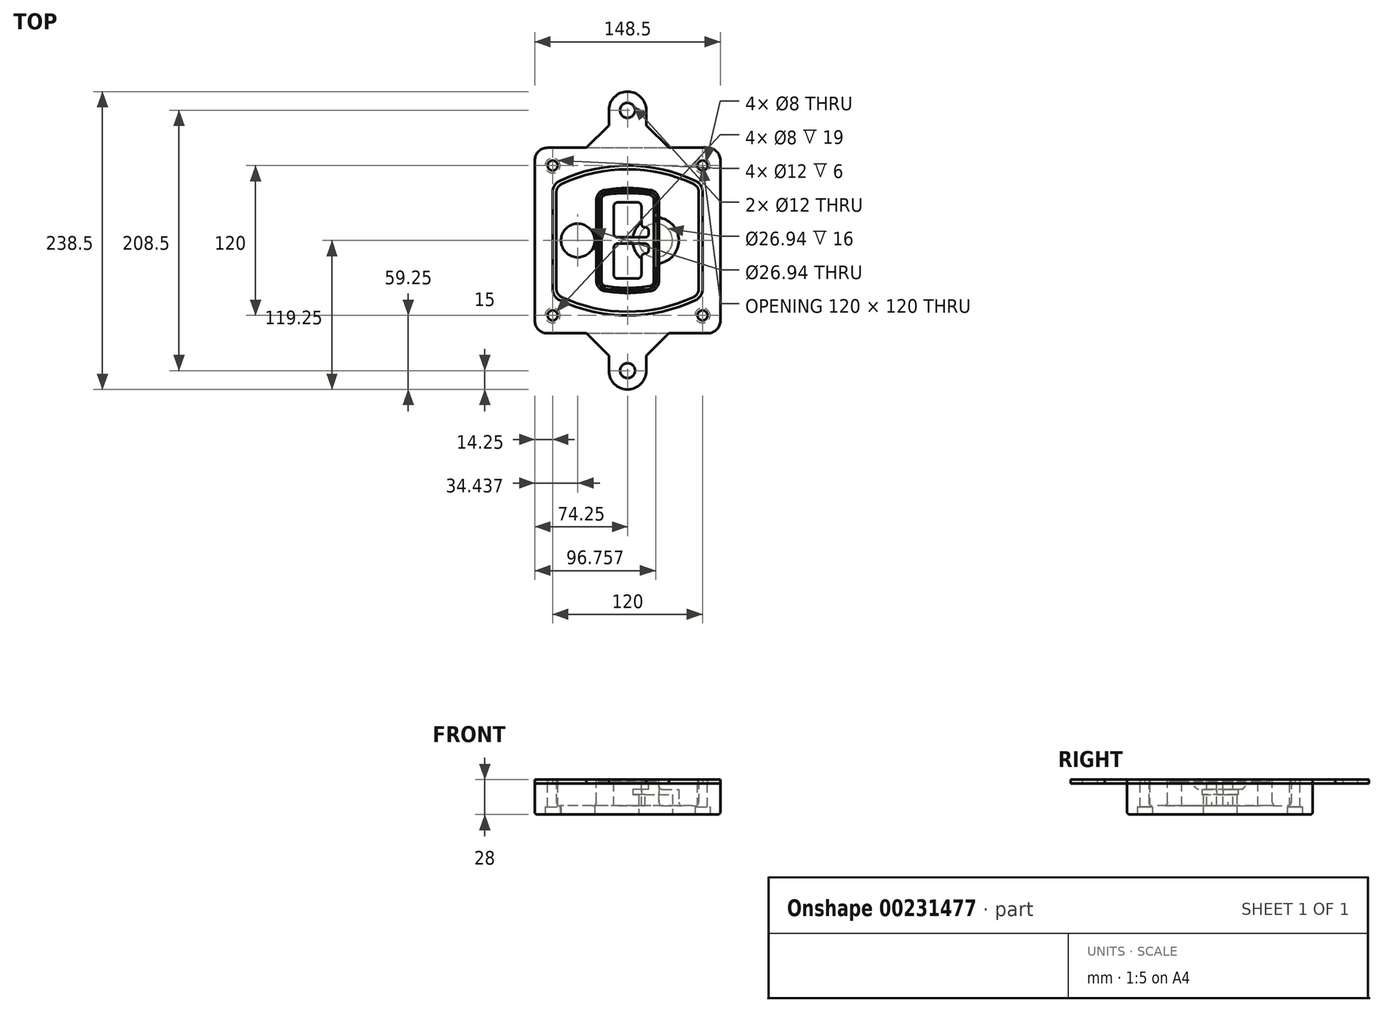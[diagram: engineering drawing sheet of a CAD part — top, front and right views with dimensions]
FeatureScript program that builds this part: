
annotation { "Feature Type Name" : "Feature", "Feature Type Description" : "" }
export const myFeature = defineFeature(function(context is Context, id is Id, definition is map)
    precondition{}
    {
        {
            var Q0;
            Q0=qCreatedBy(makeId("Top.planeOp"),FACE);
            var sketch = newSketch(context, id + "F0", { "sketchPlane" : qUnion([Q0])});
            skPoint(sketch, "E0.rect.middle", {"position": v(0, 0) * mm});
            skLineSegment(sketch, "E1.bottom", {"start": v(-64.25, -74.25) * mm, "end": v(64.25, -74.25) * mm});
            skLineSegment(sketch, "E1.top", {"start": v(-64.25, 74.25) * mm, "end": v(64.25, 74.25) * mm});
            skLineSegment(sketch, "E1.left", {"start": v(-74.25, -64.25) * mm, "end": v(-74.25, 64.25) * mm});
            skLineSegment(sketch, "E1.right", {"start": v(74.25, -64.25) * mm, "end": v(74.25, 64.25) * mm});
            skLineSegment(sketch, "E2", {"start": v(-74.25, 74.25) * mm, "end": v(74.25, -74.25) * mm, "construction": true});
            skLineSegment(sketch, "E3", {"start": v(74.25, 74.25) * mm, "end": v(-74.25, -74.25) * mm, "construction": true});
            skCircle(sketch, "E4", {"center": v(-60, 60) * mm, "radius": 4 * mm});
            skCircle(sketch, "E5", {"center": v(60, 60) * mm, "radius": 4 * mm});
            skCircle(sketch, "E6", {"center": v(60, -60) * mm, "radius": 4 * mm});
            skCircle(sketch, "E7", {"center": v(-60, -60) * mm, "radius": 4 * mm});
            skLineSegment(sketch, "E8", {"start": v(-60, 60) * mm, "end": v(60, 60) * mm, "construction": true});
            skLineSegment(sketch, "E9", {"start": v(60, 60) * mm, "end": v(60, -60) * mm, "construction": true});
            skLineSegment(sketch, "E10", {"start": v(60, -60) * mm, "end": v(-60, -60) * mm, "construction": true});
            skLineSegment(sketch, "E11", {"start": v(-60, -60) * mm, "end": v(-60, 60) * mm, "construction": true});
            skLineSegment(sketch, "E12", {"start": v(-60, 38.83) * mm, "end": v(-60, -38.83) * mm});
            skLineSegment(sketch, "E13", {"start": v(60, 38.83) * mm, "end": v(60, -38.83) * mm});
            skArc(sketch, "E14", {"start": v(54.26, 47.88) * mm, "mid": v(0, 60) * mm, "end": v(-54.26, 47.88) * mm});
            skArc(sketch, "E15", {"start": v(-54.26, -47.88) * mm, "mid": v(0, -60) * mm, "end": v(54.26, -47.88) * mm});
            skLineSegment(sketch, "E16", {"start": v(-60, 0) * mm, "end": v(60, 0) * mm, "construction": true});
            skPoint(sketch, "E17.visualSharp", {"position": v(-60, -45) * mm});
            skArc(sketch, "E17.filletArc", {"start": v(-60, -38.83) * mm, "mid": v(-58.44, -44.2) * mm, "end": v(-54.26, -47.88) * mm});
            skPoint(sketch, "E18.visualSharp", {"position": v(-60, 45) * mm});
            skArc(sketch, "E18.filletArc", {"start": v(-54.26, 47.88) * mm, "mid": v(-58.44, 44.2) * mm, "end": v(-60, 38.83) * mm});
            skPoint(sketch, "E19.visualSharp", {"position": v(60, 45) * mm});
            skArc(sketch, "E19.filletArc", {"start": v(60, 38.83) * mm, "mid": v(58.44, 44.2) * mm, "end": v(54.26, 47.88) * mm});
            skPoint(sketch, "E20.visualSharp", {"position": v(60, -45) * mm});
            skArc(sketch, "E20.filletArc", {"start": v(54.26, -47.88) * mm, "mid": v(58.44, -44.2) * mm, "end": v(60, -38.83) * mm});
            skPoint(sketch, "E21.visualSharp", {"position": v(-74.25, 74.25) * mm});
            skArc(sketch, "E21.filletArc", {"start": v(-64.25, 74.25) * mm, "mid": v(-71.32, 71.32) * mm, "end": v(-74.25, 64.25) * mm});
            skPoint(sketch, "E22.visualSharp", {"position": v(74.25, 74.25) * mm});
            skArc(sketch, "E22.filletArc", {"start": v(74.25, 64.25) * mm, "mid": v(71.32, 71.32) * mm, "end": v(64.25, 74.25) * mm});
            skPoint(sketch, "E23.visualSharp", {"position": v(74.25, -74.25) * mm});
            skArc(sketch, "E23.filletArc", {"start": v(64.25, -74.25) * mm, "mid": v(71.32, -71.32) * mm, "end": v(74.25, -64.25) * mm});
            skPoint(sketch, "E24.visualSharp", {"position": v(-74.25, -74.25) * mm});
            skArc(sketch, "E24.filletArc", {"start": v(-74.25, -64.25) * mm, "mid": v(-71.32, -71.32) * mm, "end": v(-64.25, -74.25) * mm});
            skArc(sketch, "E25.0", {"start": v(57, 38.83) * mm, "mid": v(55.9, 42.58) * mm, "end": v(52.98, 45.17) * mm});
            skLineSegment(sketch, "E25.1", {"start": v(57, 38.83) * mm, "end": v(57, -38.83) * mm});
            skArc(sketch, "E25.2", {"start": v(52.98, -45.17) * mm, "mid": v(55.9, -42.58) * mm, "end": v(57, -38.83) * mm});
            skArc(sketch, "E25.3", {"start": v(-52.98, -45.17) * mm, "mid": v(0, -57) * mm, "end": v(52.98, -45.17) * mm});
            skArc(sketch, "E25.4", {"start": v(-57, -38.83) * mm, "mid": v(-55.9, -42.58) * mm, "end": v(-52.98, -45.17) * mm});
            skArc(sketch, "E25.5", {"start": v(52.98, 45.17) * mm, "mid": v(0, 57) * mm, "end": v(-52.98, 45.17) * mm});
            skLineSegment(sketch, "E25.6", {"start": v(-57, 38.83) * mm, "end": v(-57, -38.83) * mm});
            skArc(sketch, "E25.7", {"start": v(-52.98, 45.17) * mm, "mid": v(-55.9, 42.58) * mm, "end": v(-57, 38.83) * mm});
            skArc(sketch, "E26.0", {"start": v(-55.96, 51.5) * mm, "mid": v(-61.82, 46.33) * mm, "end": v(-64, 38.83) * mm});
            skArc(sketch, "E26.1", {"start": v(55.96, 51.5) * mm, "mid": v(0, 64) * mm, "end": v(-55.96, 51.5) * mm});
            skArc(sketch, "E26.2", {"start": v(64, 38.83) * mm, "mid": v(61.82, 46.33) * mm, "end": v(55.96, 51.5) * mm});
            skLineSegment(sketch, "E26.3", {"start": v(64, 38.83) * mm, "end": v(64, -38.83) * mm});
            skArc(sketch, "E26.4", {"start": v(55.96, -51.5) * mm, "mid": v(61.82, -46.33) * mm, "end": v(64, -38.83) * mm});
            skLineSegment(sketch, "E26.5", {"start": v(-64, 38.83) * mm, "end": v(-64, -38.83) * mm});
            skArc(sketch, "E26.6", {"start": v(-55.96, -51.5) * mm, "mid": v(0, -64) * mm, "end": v(55.96, -51.5) * mm});
            skArc(sketch, "E26.7", {"start": v(-64, -38.83) * mm, "mid": v(-61.82, -46.33) * mm, "end": v(-55.96, -51.5) * mm});
            skSolve(sketch);
        }
        {
            var Q0;
            Q0=makeQuery(id+"F0.imprint","IMPRINT",FACE,{"disambiguationData":[TD([[makeQuery(id+"F0.imprint","IMPRINT",EDGE,{"derivedFrom":sQuery(id+"F0.wireOp",EDGE,"E1.bottom")}),1.0]])]});
            var Q1;
            Q1=makeQuery(id+"F0.imprint","IMPRINT",FACE,{"disambiguationData":[TD([[makeQuery(id+"F0.imprint","IMPRINT",EDGE,{"derivedFrom":sQuery(id+"F0.wireOp",EDGE,"E12")}),1.0]])]});
            var Q2;
            Q2=makeQuery(id+"F0.imprint","IMPRINT",FACE,{"disambiguationData":[TD([[makeQuery(id+"F0.imprint","IMPRINT",EDGE,{"derivedFrom":sQuery(id+"F0.wireOp",EDGE,"E25.0")}),1.0]])]});
            var Q3;
            Q3=makeQuery(id+"F0.imprint","IMPRINT",FACE,{"disambiguationData":[TD([[makeQuery(id+"F0.imprint","IMPRINT",EDGE,{"derivedFrom":sQuery(id+"F0.wireOp",EDGE,"E12")}),-1.0]])]});
            extrude(context, id + "F1", {"entities" : qUnion([Q0, Q1, Q2, Q3]), "oppositeDirection" : true, "depth" : 25 * mm});
        }
        {
            var Q0;
            Q0=makeQuery(id+"F0.imprint","IMPRINT",FACE,{"disambiguationData":[TD([[makeQuery(id+"F0.imprint","IMPRINT",EDGE,{"derivedFrom":sQuery(id+"F0.wireOp",EDGE,"E12")}),1.0]])]});
            extrude(context, id + "F2", {"entities" : qUnion([Q0]), "operationType" : NewBodyOperationType.ADD, "depth" : 3 * mm});
        }
        {
            var Q0;
            Q0=makeQuery(id+"F0.imprint","IMPRINT",FACE,{"disambiguationData":[TD([[makeQuery(id+"F0.imprint","IMPRINT",EDGE,{"derivedFrom":sQuery(id+"F0.wireOp",EDGE,"E25.0")}),1.0]])]});
            extrude(context, id + "F3", {"entities" : qUnion([Q0]), "operationType" : NewBodyOperationType.REMOVE, "oppositeDirection" : true, "depth" : 18 * mm});
        }
        {
            var Q0;
            Q0=makeQuery(id+"F2.opExtrude","CAP_FACE",FACE,{"disambiguationData":[OSD([sQuery(id+"F0.wireOp",EDGE,"E12"),sQuery(id+"F0.wireOp",EDGE,"E13"),sQuery(id+"F0.wireOp",EDGE,"E14"),sQuery(id+"F0.wireOp",EDGE,"E15"),sQuery(id+"F0.wireOp",EDGE,"E17.filletArc"),sQuery(id+"F0.wireOp",EDGE,"E18.filletArc"),sQuery(id+"F0.wireOp",EDGE,"E19.filletArc"),sQuery(id+"F0.wireOp",EDGE,"E20.filletArc"),sQuery(id+"F0.wireOp",EDGE,"E25.0"),sQuery(id+"F0.wireOp",EDGE,"E25.1"),sQuery(id+"F0.wireOp",EDGE,"E25.2"),sQuery(id+"F0.wireOp",EDGE,"E25.3"),sQuery(id+"F0.wireOp",EDGE,"E25.4"),sQuery(id+"F0.wireOp",EDGE,"E25.5"),sQuery(id+"F0.wireOp",EDGE,"E25.6"),sQuery(id+"F0.wireOp",EDGE,"E25.7")])],"isStart":false});
            var sketch = newSketch(context, id + "F4", { "sketchPlane" : qUnion([Q0])});
            skArc(sketch, "E27.0", {"start": v(-18.34, -40.45) * mm, "mid": v(0, -42) * mm, "end": v(18.34, -40.45) * mm});
            skArc(sketch, "E28.0", {"start": v(18.34, 40.45) * mm, "mid": v(0, 42) * mm, "end": v(-18.34, 40.45) * mm});
            skLineSegment(sketch, "E29", {"start": v(-25, 32.57) * mm, "end": v(-25, -32.57) * mm});
            skLineSegment(sketch, "E30", {"start": v(25, 32.57) * mm, "end": v(25, -32.57) * mm});
            skLineSegment(sketch, "E31", {"start": v(-25, 39.1) * mm, "end": v(25, 39.1) * mm, "construction": true});
            skLineSegment(sketch, "E32", {"start": v(-25, -39.1) * mm, "end": v(25, -39.1) * mm, "construction": true});
            skPoint(sketch, "E33.visualSharp", {"position": v(-25, 39.1) * mm});
            skArc(sketch, "E33.filletArc", {"start": v(-18.34, 40.45) * mm, "mid": v(-23.11, 37.73) * mm, "end": v(-25, 32.57) * mm});
            skPoint(sketch, "E34.visualSharp", {"position": v(25, 39.1) * mm});
            skArc(sketch, "E34.filletArc", {"start": v(25, 32.57) * mm, "mid": v(23.11, 37.73) * mm, "end": v(18.34, 40.45) * mm});
            skPoint(sketch, "E35.visualSharp", {"position": v(25, -39.1) * mm});
            skArc(sketch, "E35.filletArc", {"start": v(18.34, -40.45) * mm, "mid": v(23.11, -37.73) * mm, "end": v(25, -32.57) * mm});
            skPoint(sketch, "E36.visualSharp", {"position": v(-25, -39.1) * mm});
            skArc(sketch, "E36.filletArc", {"start": v(-25, -32.57) * mm, "mid": v(-23.11, -37.73) * mm, "end": v(-18.34, -40.45) * mm});
            skArc(sketch, "E37.0", {"start": v(52.98, 45.17) * mm, "mid": v(0, 57) * mm, "end": v(-52.98, 45.17) * mm});
            skArc(sketch, "E37.1", {"start": v(-52.98, 45.17) * mm, "mid": v(-55.9, 42.58) * mm, "end": v(-57, 38.83) * mm});
            skLineSegment(sketch, "E37.2", {"start": v(-57, 38.83) * mm, "end": v(-57, -38.83) * mm});
            skArc(sketch, "E37.3", {"start": v(-57, -38.83) * mm, "mid": v(-55.9, -42.58) * mm, "end": v(-52.98, -45.17) * mm});
            skArc(sketch, "E37.4", {"start": v(-52.98, -45.17) * mm, "mid": v(0, -57) * mm, "end": v(52.98, -45.17) * mm});
            skArc(sketch, "E37.5", {"start": v(52.98, -45.17) * mm, "mid": v(55.9, -42.58) * mm, "end": v(57, -38.83) * mm});
            skLineSegment(sketch, "E37.6", {"start": v(57, 38.83) * mm, "end": v(57, -38.83) * mm});
            skArc(sketch, "E37.7", {"start": v(57, 38.83) * mm, "mid": v(55.9, 42.58) * mm, "end": v(52.98, 45.17) * mm});
            skLineSegment(sketch, "E38.0", {"start": v(23, 32.57) * mm, "end": v(23, -32.57) * mm});
            skArc(sketch, "E38.1", {"start": v(18, -38.48) * mm, "mid": v(21.58, -36.44) * mm, "end": v(23, -32.57) * mm});
            skArc(sketch, "E38.2", {"start": v(-18, -38.48) * mm, "mid": v(0, -40) * mm, "end": v(18, -38.48) * mm});
            skArc(sketch, "E38.3", {"start": v(-23, -32.57) * mm, "mid": v(-21.58, -36.44) * mm, "end": v(-18, -38.48) * mm});
            skLineSegment(sketch, "E38.4", {"start": v(-23, 32.57) * mm, "end": v(-23, -32.57) * mm});
            skArc(sketch, "E38.5", {"start": v(23, 32.57) * mm, "mid": v(21.58, 36.44) * mm, "end": v(18, 38.48) * mm});
            skArc(sketch, "E38.6", {"start": v(-18, 38.48) * mm, "mid": v(-21.58, 36.44) * mm, "end": v(-23, 32.57) * mm});
            skArc(sketch, "E38.7", {"start": v(18, 38.48) * mm, "mid": v(0, 40) * mm, "end": v(-18, 38.48) * mm});
            skArc(sketch, "E39.0", {"start": v(21, 32.57) * mm, "mid": v(20.06, 35.15) * mm, "end": v(17.67, 36.5) * mm});
            skLineSegment(sketch, "E39.1", {"start": v(21, 32.57) * mm, "end": v(21, -32.57) * mm});
            skArc(sketch, "E39.2", {"start": v(17.67, -36.5) * mm, "mid": v(20.06, -35.15) * mm, "end": v(21, -32.57) * mm});
            skArc(sketch, "E39.3", {"start": v(-17.67, -36.5) * mm, "mid": v(0, -38) * mm, "end": v(17.67, -36.5) * mm});
            skArc(sketch, "E39.4", {"start": v(-21, -32.57) * mm, "mid": v(-20.06, -35.15) * mm, "end": v(-17.67, -36.5) * mm});
            skArc(sketch, "E39.5", {"start": v(17.67, 36.5) * mm, "mid": v(0, 38) * mm, "end": v(-17.67, 36.5) * mm});
            skLineSegment(sketch, "E39.6", {"start": v(-21, 32.57) * mm, "end": v(-21, -32.57) * mm});
            skArc(sketch, "E39.7", {"start": v(-17.67, 36.5) * mm, "mid": v(-20.06, 35.15) * mm, "end": v(-21, 32.57) * mm});
            skLineSegment(sketch, "E40", {"start": v(-25, 0) * mm, "end": v(25, 0) * mm, "construction": true});
            skLineSegment(sketch, "E41", {"start": v(-11, 5.5) * mm, "end": v(-11, 27.5) * mm});
            skLineSegment(sketch, "E42", {"start": v(-8, 30.5) * mm, "end": v(8, 30.5) * mm});
            skLineSegment(sketch, "E43", {"start": v(11, 27.5) * mm, "end": v(11, 13.5) * mm});
            skLineSegment(sketch, "E44", {"start": v(14, 10.5) * mm, "end": v(14, 10.5) * mm});
            skLineSegment(sketch, "E45", {"start": v(17, 7.5) * mm, "end": v(17, 5.5) * mm});
            skLineSegment(sketch, "E46", {"start": v(14, 2.5) * mm, "end": v(-8, 2.5) * mm});
            skPoint(sketch, "E47.visualSharp", {"position": v(-11, 30.5) * mm});
            skArc(sketch, "E47.filletArc", {"start": v(-8, 30.5) * mm, "mid": v(-10.12, 29.62) * mm, "end": v(-11, 27.5) * mm});
            skPoint(sketch, "E48.visualSharp", {"position": v(11, 30.5) * mm});
            skArc(sketch, "E48.filletArc", {"start": v(11, 27.5) * mm, "mid": v(10.12, 29.62) * mm, "end": v(8, 30.5) * mm});
            skPoint(sketch, "E49.visualSharp", {"position": v(11, 10.5) * mm});
            skArc(sketch, "E49.filletArc", {"start": v(11, 13.5) * mm, "mid": v(11.88, 11.38) * mm, "end": v(14, 10.5) * mm});
            skPoint(sketch, "E50.visualSharp", {"position": v(17, 10.5) * mm});
            skArc(sketch, "E50.filletArc", {"start": v(17, 7.5) * mm, "mid": v(16.12, 9.62) * mm, "end": v(14, 10.5) * mm});
            skPoint(sketch, "E51.visualSharp", {"position": v(17, 2.5) * mm});
            skArc(sketch, "E51.filletArc", {"start": v(14, 2.5) * mm, "mid": v(16.12, 3.38) * mm, "end": v(17, 5.5) * mm});
            skPoint(sketch, "E52.visualSharp", {"position": v(-11, 2.5) * mm});
            skArc(sketch, "E52.filletArc", {"start": v(-11, 5.5) * mm, "mid": v(-10.12, 3.38) * mm, "end": v(-8, 2.5) * mm});
            skLineSegment(sketch, "E53.0.MirrorCS", {"start": v(14, -2.5) * mm, "end": v(-8, -2.5) * mm});
            skArc(sketch, "E54.0.MirrorCS", {"start": v(-11, -5.5) * mm, "mid": v(-10.12, -3.38) * mm, "end": v(-8, -2.5) * mm});
            skLineSegment(sketch, "E55.0.MirrorCS", {"start": v(-11, -5.5) * mm, "end": v(-11, -27.5) * mm});
            skArc(sketch, "E56.0.MirrorCS", {"start": v(-8, -30.5) * mm, "mid": v(-10.12, -29.62) * mm, "end": v(-11, -27.5) * mm});
            skLineSegment(sketch, "E57.0.MirrorCS", {"start": v(-8, -30.5) * mm, "end": v(8, -30.5) * mm});
            skArc(sketch, "E58.0.MirrorCS", {"start": v(11, -27.5) * mm, "mid": v(10.12, -29.62) * mm, "end": v(8, -30.5) * mm});
            skLineSegment(sketch, "E59.0.MirrorCS", {"start": v(11, -27.5) * mm, "end": v(11, -13.5) * mm});
            skArc(sketch, "E60.0.MirrorCS", {"start": v(11, -13.5) * mm, "mid": v(11.88, -11.38) * mm, "end": v(14, -10.5) * mm});
            skArc(sketch, "E61.0.MirrorCS", {"start": v(17, -7.5) * mm, "mid": v(16.12, -9.62) * mm, "end": v(14, -10.5) * mm});
            skLineSegment(sketch, "E62.0.MirrorCS", {"start": v(17, -7.5) * mm, "end": v(17, -5.5) * mm});
            skArc(sketch, "E63.0.MirrorCS", {"start": v(14, -2.5) * mm, "mid": v(16.12, -3.38) * mm, "end": v(17, -5.5) * mm});
            skSolve(sketch);
        }
        {
            var Q0;
            Q0=makeQuery(id+"F4.imprint","IMPRINT",FACE,{"disambiguationData":[TD([[makeQuery(id+"F4.imprint","IMPRINT",EDGE,{"derivedFrom":sQuery(id+"F4.wireOp",EDGE,"E27.0")}),1.0]])]});
            var Q1;
            Q1=makeQuery(id+"F4.imprint","IMPRINT",FACE,{"disambiguationData":[TD([[makeQuery(id+"F4.imprint","IMPRINT",EDGE,{"derivedFrom":sQuery(id+"F4.wireOp",EDGE,"E38.0")}),-1.0]])]});
            var Q2;
            Q2=makeQuery(id+"F4.imprint","IMPRINT",FACE,{"disambiguationData":[TD([[makeQuery(id+"F4.imprint","IMPRINT",EDGE,{"derivedFrom":sQuery(id+"F4.wireOp",EDGE,"E39.0")}),1.0]])]});
            extrude(context, id + "F5", {"entities" : qUnion([Q0, Q1, Q2]), "operationType" : NewBodyOperationType.ADD, "endBound" : BoundingType.UP_TO_NEXT, "oppositeDirection" : true, "depth" : 25 * mm});
        }
        {
            var Q0;
            Q0=makeQuery(id+"F4.imprint","IMPRINT",FACE,{"disambiguationData":[TD([[makeQuery(id+"F4.imprint","IMPRINT",EDGE,{"derivedFrom":sQuery(id+"F4.wireOp",EDGE,"E38.0")}),-1.0]])]});
            extrude(context, id + "F6", {"entities" : qUnion([Q0]), "operationType" : NewBodyOperationType.REMOVE, "oppositeDirection" : true, "depth" : 2 * mm});
        }
        {
            var Q0;
            Q0=makeQuery(id+"F1.opExtrude","CAP_FACE",FACE,{"disambiguationData":[OSD([sQuery(id+"F0.wireOp",EDGE,"E1.bottom"),sQuery(id+"F0.wireOp",EDGE,"E1.top"),sQuery(id+"F0.wireOp",EDGE,"E1.left"),sQuery(id+"F0.wireOp",EDGE,"E1.right"),sQuery(id+"F0.wireOp",EDGE,"E4"),sQuery(id+"F0.wireOp",EDGE,"E5"),sQuery(id+"F0.wireOp",EDGE,"E6"),sQuery(id+"F0.wireOp",EDGE,"E7"),sQuery(id+"F0.wireOp",EDGE,"E21.filletArc"),sQuery(id+"F0.wireOp",EDGE,"E22.filletArc"),sQuery(id+"F0.wireOp",EDGE,"E23.filletArc"),sQuery(id+"F0.wireOp",EDGE,"E24.filletArc")])],"isStart":false});
            var sketch = newSketch(context, id + "F7", { "sketchPlane" : qUnion([Q0])});
            skCircle(sketch, "E64", {"center": v(22.5, 0) * mm, "radius": 13.47 * mm});
            skCircle(sketch, "E65", {"center": v(-39.81, 0) * mm, "radius": 13.47 * mm});
            skLineSegment(sketch, "E66", {"start": v(74.25, 0) * mm, "end": v(-74.25, 0) * mm});
            skCircle(sketch, "E67", {"center": v(22.5, 0) * mm, "radius": 18.47 * mm});
            skCircle(sketch, "E68", {"center": v(60, -60) * mm, "radius": 6 * mm});
            skCircle(sketch, "E69", {"center": v(-60, -60) * mm, "radius": 6 * mm});
            skCircle(sketch, "E70", {"center": v(-60, 60) * mm, "radius": 6 * mm});
            skCircle(sketch, "E71", {"center": v(60, 60) * mm, "radius": 6 * mm});
            skSolve(sketch);
        }
        {
            var Q0;
            {var subQ1=sQuery(id+"F7.wireOp",EDGE,"E66");var subQ4=sQuery(id+"F7.wireOp",EDGE,"E64");var subQ6=makeQuery(id+"F7.imprint","INTERSECT",VERTEX,{"disambiguationData":[OD(0.0)],"derivedFrom":[subQ4,subQ1]});Q0=makeQuery(id+"F7.imprint","IMPRINT",FACE,{"disambiguationData":[TD([[makeQuery(id+"F7.imprint","IMPRINT",EDGE,{"disambiguationData":[TD([[subQ6,-1.0]])],"derivedFrom":subQ4}),-1.0]])]});}
            var Q1;
            {var subQ0=sQuery(id+"F7.wireOp",EDGE,"E66");var subQ1=sQuery(id+"F7.wireOp",EDGE,"E64");var subQ3=makeQuery(id+"F7.imprint","INTERSECT",VERTEX,{"disambiguationData":[OD(0.0)],"derivedFrom":[subQ1,subQ0]});Q1=makeQuery(id+"F7.imprint","IMPRINT",FACE,{"disambiguationData":[TD([[makeQuery(id+"F7.imprint","IMPRINT",EDGE,{"disambiguationData":[TD([[subQ3,-1.0]])],"derivedFrom":subQ1}),1.0]])]});}
            var Q2;
            {var subQ0=sQuery(id+"F7.wireOp",EDGE,"E66");var subQ1=sQuery(id+"F7.wireOp",EDGE,"E64");var subQ3=makeQuery(id+"F7.imprint","INTERSECT",VERTEX,{"disambiguationData":[OD(0.0)],"derivedFrom":[subQ1,subQ0]});Q2=makeQuery(id+"F7.imprint","IMPRINT",FACE,{"disambiguationData":[TD([[makeQuery(id+"F7.imprint","IMPRINT",EDGE,{"disambiguationData":[TD([[subQ3,1.0]])],"derivedFrom":subQ1}),1.0]])]});}
            var Q3;
            {var subQ1=sQuery(id+"F7.wireOp",EDGE,"E66");var subQ4=sQuery(id+"F7.wireOp",EDGE,"E64");var subQ6=makeQuery(id+"F7.imprint","INTERSECT",VERTEX,{"disambiguationData":[OD(0.0)],"derivedFrom":[subQ4,subQ1]});Q3=makeQuery(id+"F7.imprint","IMPRINT",FACE,{"disambiguationData":[TD([[makeQuery(id+"F7.imprint","IMPRINT",EDGE,{"disambiguationData":[TD([[subQ6,1.0]])],"derivedFrom":subQ4}),-1.0]])]});}
            extrude(context, id + "F8", {"entities" : qUnion([Q0, Q1, Q2, Q3]), "operationType" : NewBodyOperationType.ADD, "oppositeDirection" : true, "depth" : 20 * mm});
        }
        {
            var Q0;
            {var subQ0=sQuery(id+"F7.wireOp",EDGE,"E66");var subQ1=sQuery(id+"F7.wireOp",EDGE,"E64");var subQ3=makeQuery(id+"F7.imprint","INTERSECT",VERTEX,{"disambiguationData":[OD(0.0)],"derivedFrom":[subQ1,subQ0]});Q0=makeQuery(id+"F7.imprint","IMPRINT",FACE,{"disambiguationData":[TD([[makeQuery(id+"F7.imprint","IMPRINT",EDGE,{"disambiguationData":[TD([[subQ3,-1.0]])],"derivedFrom":subQ1}),1.0]])]});}
            var Q1;
            {var subQ0=sQuery(id+"F7.wireOp",EDGE,"E66");var subQ1=sQuery(id+"F7.wireOp",EDGE,"E64");var subQ3=makeQuery(id+"F7.imprint","INTERSECT",VERTEX,{"disambiguationData":[OD(0.0)],"derivedFrom":[subQ1,subQ0]});Q1=makeQuery(id+"F7.imprint","IMPRINT",FACE,{"disambiguationData":[TD([[makeQuery(id+"F7.imprint","IMPRINT",EDGE,{"disambiguationData":[TD([[subQ3,1.0]])],"derivedFrom":subQ1}),1.0]])]});}
            extrude(context, id + "F9", {"entities" : qUnion([Q0, Q1]), "operationType" : NewBodyOperationType.REMOVE, "oppositeDirection" : true, "depth" : 16 * mm});
        }
        {
            var Q0;
            {var subQ0=sQuery(id+"F7.wireOp",EDGE,"E66");var subQ1=sQuery(id+"F7.wireOp",EDGE,"E65");var subQ3=makeQuery(id+"F7.imprint","INTERSECT",VERTEX,{"disambiguationData":[OD(0.0)],"derivedFrom":[subQ1,subQ0]});Q0=makeQuery(id+"F7.imprint","IMPRINT",FACE,{"disambiguationData":[TD([[makeQuery(id+"F7.imprint","IMPRINT",EDGE,{"disambiguationData":[TD([[subQ3,-1.0]])],"derivedFrom":subQ1}),1.0]])]});}
            var Q1;
            {var subQ0=sQuery(id+"F7.wireOp",EDGE,"E66");var subQ1=sQuery(id+"F7.wireOp",EDGE,"E65");var subQ3=makeQuery(id+"F7.imprint","INTERSECT",VERTEX,{"disambiguationData":[OD(0.0)],"derivedFrom":[subQ1,subQ0]});Q1=makeQuery(id+"F7.imprint","IMPRINT",FACE,{"disambiguationData":[TD([[makeQuery(id+"F7.imprint","IMPRINT",EDGE,{"disambiguationData":[TD([[subQ3,1.0]])],"derivedFrom":subQ1}),1.0]])]});}
            extrude(context, id + "F10", {"entities" : qUnion([Q0, Q1]), "operationType" : NewBodyOperationType.REMOVE, "oppositeDirection" : true, "depth" : 25 * mm});
        }
        {
            var Q0;
            Q0=makeQuery(id+"F7.imprint","IMPRINT",FACE,{"disambiguationData":[TD([[makeQuery(id+"F7.imprint","IMPRINT",EDGE,{"derivedFrom":sQuery(id+"F7.wireOp",EDGE,"E68")}),1.0]])]});
            var Q1;
            Q1=makeQuery(id+"F7.imprint","IMPRINT",FACE,{"disambiguationData":[TD([[makeQuery(id+"F7.imprint","IMPRINT",EDGE,{"derivedFrom":makeQuery(id+"F1.opExtrude","CAP_EDGE",EDGE,{"disambiguationData":[OSD([sQuery(id+"F0.wireOp",EDGE,"E5")])],"isStart":false})}),-1.0]])]});
            var Q2;
            Q2=makeQuery(id+"F7.imprint","IMPRINT",FACE,{"disambiguationData":[TD([[makeQuery(id+"F7.imprint","IMPRINT",EDGE,{"derivedFrom":sQuery(id+"F7.wireOp",EDGE,"E69")}),1.0]])]});
            var Q3;
            Q3=makeQuery(id+"F7.imprint","IMPRINT",FACE,{"disambiguationData":[TD([[makeQuery(id+"F7.imprint","IMPRINT",EDGE,{"derivedFrom":makeQuery(id+"F1.opExtrude","CAP_EDGE",EDGE,{"disambiguationData":[OSD([sQuery(id+"F0.wireOp",EDGE,"E4")])],"isStart":false})}),-1.0]])]});
            var Q4;
            Q4=makeQuery(id+"F7.imprint","IMPRINT",FACE,{"disambiguationData":[TD([[makeQuery(id+"F7.imprint","IMPRINT",EDGE,{"derivedFrom":sQuery(id+"F7.wireOp",EDGE,"E70")}),1.0]])]});
            var Q5;
            Q5=makeQuery(id+"F7.imprint","IMPRINT",FACE,{"disambiguationData":[TD([[makeQuery(id+"F7.imprint","IMPRINT",EDGE,{"derivedFrom":makeQuery(id+"F1.opExtrude","CAP_EDGE",EDGE,{"disambiguationData":[OSD([sQuery(id+"F0.wireOp",EDGE,"E7")])],"isStart":false})}),-1.0]])]});
            var Q6;
            Q6=makeQuery(id+"F7.imprint","IMPRINT",FACE,{"disambiguationData":[TD([[makeQuery(id+"F7.imprint","IMPRINT",EDGE,{"derivedFrom":sQuery(id+"F7.wireOp",EDGE,"E71")}),1.0]])]});
            var Q7;
            Q7=makeQuery(id+"F7.imprint","IMPRINT",FACE,{"disambiguationData":[TD([[makeQuery(id+"F7.imprint","IMPRINT",EDGE,{"derivedFrom":makeQuery(id+"F1.opExtrude","CAP_EDGE",EDGE,{"disambiguationData":[OSD([sQuery(id+"F0.wireOp",EDGE,"E6")])],"isStart":false})}),-1.0]])]});
            extrude(context, id + "F11", {"entities" : qUnion([Q0, Q1, Q2, Q3, Q4, Q5, Q6, Q7]), "operationType" : NewBodyOperationType.REMOVE, "oppositeDirection" : true, "depth" : 6 * mm});
        }
        {
            var Q0;
            Q0=makeQuery(id+"F9.boolean.opBoolean","COPY",FACE,{"derivedFrom":makeQuery(id+"F9.opExtrude","CAP_FACE",FACE,{"disambiguationData":[OSD([sQuery(id+"F7.wireOp",EDGE,"E64")])],"isStart":false})});
            var sketch = newSketch(context, id + "F12", { "sketchPlane" : qUnion([Q0])});
            skArc(sketch, "E72.0", {"start": v(11, 14.45) * mm, "mid": v(6.45, 9.13) * mm, "end": v(4.2, 2.5) * mm});
            skArc(sketch, "E72.1", {"start": v(4.2, -2.5) * mm, "mid": v(6.45, -9.13) * mm, "end": v(11, -14.45) * mm});
            skLineSegment(sketch, "E73", {"start": v(4.2, -2.5) * mm, "end": v(14, -2.5) * mm});
            skLineSegment(sketch, "E74.0", {"start": v(14, 2.5) * mm, "end": v(4.2, 2.5) * mm});
            skArc(sketch, "E74.1", {"start": v(14, 2.5) * mm, "mid": v(16.12, 3.38) * mm, "end": v(17, 5.5) * mm});
            skLineSegment(sketch, "E74.2", {"start": v(17, 7.5) * mm, "end": v(17, 5.5) * mm});
            skArc(sketch, "E74.3", {"start": v(17, 7.5) * mm, "mid": v(16.12, 9.62) * mm, "end": v(14, 10.5) * mm});
            skArc(sketch, "E74.4", {"start": v(11, 13.5) * mm, "mid": v(11.88, 11.38) * mm, "end": v(14, 10.5) * mm});
            skLineSegment(sketch, "E74.5", {"start": v(11, 14.45) * mm, "end": v(11, 13.5) * mm});
            skLineSegment(sketch, "E74.7", {"start": v(14, -2.5) * mm, "end": v(4.2, -2.5) * mm});
            skArc(sketch, "E74.8", {"start": v(14, -2.5) * mm, "mid": v(16.12, -3.38) * mm, "end": v(17, -5.5) * mm});
            skLineSegment(sketch, "E74.9", {"start": v(17, -7.5) * mm, "end": v(17, -5.5) * mm});
            skArc(sketch, "E74.10", {"start": v(17, -7.5) * mm, "mid": v(16.12, -9.62) * mm, "end": v(14, -10.5) * mm});
            skArc(sketch, "E74.11", {"start": v(11, -13.5) * mm, "mid": v(11.88, -11.38) * mm, "end": v(14, -10.5) * mm});
            skLineSegment(sketch, "E74.12", {"start": v(11, -14.45) * mm, "end": v(11, -13.5) * mm});
            skPoint(sketch, "E75.orphan", {"position": v(11, -27.5) * mm});
            skPoint(sketch, "E76.orphan", {"position": v(-8, -2.5) * mm});
            skPoint(sketch, "E77.orphan", {"position": v(-8, 2.5) * mm});
            skPoint(sketch, "E78.orphan", {"position": v(11, 27.5) * mm});
            skSolve(sketch);
        }
        {
            var Q0;
            {var subQ7=sQuery(id+"F12.wireOp",EDGE,"E72.0");var subQ14=sQuery(id+"F12.wireOp",EDGE,"E72.1");var subQ16=sQuery(id+"F12.wireOp",EDGE,"E74.1");var subQ18=sQuery(id+"F12.wireOp",EDGE,"E74.8");Q0=qUnion([makeQuery(id+"F12.imprint","IMPRINT",FACE,{"disambiguationData":[TD([[makeQuery(id+"F12.imprint","IMPRINT",EDGE,{"derivedFrom":subQ7}),1.0]])]}),makeQuery(id+"F12.imprint","IMPRINT",FACE,{"disambiguationData":[TD([[makeQuery(id+"F12.imprint","IMPRINT",EDGE,{"derivedFrom":subQ14}),1.0]])]}),makeQuery(id+"F12.imprint","IMPRINT",FACE,{"disambiguationData":[TD([[makeQuery(id+"F12.imprint","IMPRINT",EDGE,{"derivedFrom":subQ16}),1.0]])]}),makeQuery(id+"F12.imprint","IMPRINT",FACE,{"disambiguationData":[TD([[makeQuery(id+"F12.imprint","IMPRINT",EDGE,{"derivedFrom":subQ18}),-1.0]])]})]);}
            var Q1;
            Q1=makeQuery(id+"F5.boolean.opBoolean","SPLIT",FACE,{"disambiguationData":[TD([makeQuery(id+"F5.opExtrude","SWEPT_FACE",FACE,{"disambiguationData":[OSD([sQuery(id+"F4.wireOp",EDGE,"E41")])]})])],"derivedFrom":makeQuery(id+"F3.boolean.opBoolean","COPY",FACE,{"derivedFrom":makeQuery(id+"F3.opExtrude","CAP_FACE",FACE,{"disambiguationData":[OSD([sQuery(id+"F0.wireOp",EDGE,"E25.0"),sQuery(id+"F0.wireOp",EDGE,"E25.1"),sQuery(id+"F0.wireOp",EDGE,"E25.2"),sQuery(id+"F0.wireOp",EDGE,"E25.3"),sQuery(id+"F0.wireOp",EDGE,"E25.4"),sQuery(id+"F0.wireOp",EDGE,"E25.5"),sQuery(id+"F0.wireOp",EDGE,"E25.6"),sQuery(id+"F0.wireOp",EDGE,"E25.7")])],"isStart":false})})});
            extrude(context, id + "F13", {"entities" : qUnion([Q0]), "operationType" : NewBodyOperationType.REMOVE, "endBound" : BoundingType.UP_TO_SURFACE, "endBoundEntityFace" : qUnion([Q1]), "depth" : 25 * mm});
        }
        {
            var Q0;
            Q0=makeQuery(id+"F3.boolean.opBoolean","COPY",EDGE,{"derivedFrom":makeQuery(id+"F3.opExtrude","CAP_EDGE",EDGE,{"disambiguationData":[OSD([sQuery(id+"F0.wireOp",EDGE,"E25.6")])],"isStart":false})});
            var Q1;
            Q1=makeQuery(id+"F8.boolean.opBoolean","INTERSECT",EDGE,{"derivedFrom":[makeQuery(id+"F5.opExtrude","SWEPT_FACE",FACE,{"disambiguationData":[OSD([sQuery(id+"F4.wireOp",EDGE,"E30")])]}),makeQuery(id+"F8.opExtrude","CAP_FACE",FACE,{"disambiguationData":[OSD([sQuery(id+"F7.wireOp",EDGE,"E67")])],"isStart":false})]});
            var Q2;
            Q2=makeQuery(id+"F8.boolean.opBoolean","INTERSECT",EDGE,{"disambiguationData":[OD(1.0)],"derivedFrom":[makeQuery(id+"F5.opExtrude","SWEPT_FACE",FACE,{"disambiguationData":[OSD([sQuery(id+"F4.wireOp",EDGE,"E30")])]}),makeQuery(id+"F8.opExtrude","SWEPT_FACE",FACE,{"disambiguationData":[OSD([sQuery(id+"F7.wireOp",EDGE,"E67")])]})]});
            var Q3;
            {var subQ0=sQuery(id+"F4.wireOp",EDGE,"E30");Q3=makeQuery(id+"F8.boolean.opBoolean","SPLIT",EDGE,{"disambiguationData":[TD([makeQuery(id+"F5.opExtrude","SWEPT_FACE",FACE,{"disambiguationData":[OSD([sQuery(id+"F4.wireOp",EDGE,"E35.filletArc")])]})])],"derivedFrom":makeQuery(id+"F5.opExtrude","CAP_EDGE",EDGE,{"disambiguationData":[OSD([subQ0])],"isStart":false})});}
            var Q4;
            {var subQ0=sQuery(id+"F0.wireOp",EDGE,"E25.7");var subQ1=sQuery(id+"F0.wireOp",EDGE,"E25.1");var subQ2=sQuery(id+"F0.wireOp",EDGE,"E25.6");var subQ3=sQuery(id+"F0.wireOp",EDGE,"E25.5");var subQ4=sQuery(id+"F0.wireOp",EDGE,"E25.4");var subQ5=sQuery(id+"F0.wireOp",EDGE,"E25.0");var subQ6=sQuery(id+"F0.wireOp",EDGE,"E25.2");var subQ7=sQuery(id+"F0.wireOp",EDGE,"E25.3");Q4=makeQuery(id+"F8.boolean.opBoolean","INTERSECT",EDGE,{"derivedFrom":[makeQuery(id+"F5.boolean.opBoolean","SPLIT",FACE,{"disambiguationData":[TD([makeQuery(id+"F2.opExtrude","SWEPT_FACE",FACE,{"disambiguationData":[OSD([subQ5])]})])],"derivedFrom":makeQuery(id+"F3.boolean.opBoolean","COPY",FACE,{"derivedFrom":makeQuery(id+"F3.opExtrude","CAP_FACE",FACE,{"disambiguationData":[OSD([subQ5,subQ1,subQ6,subQ7,subQ4,subQ3,subQ2,subQ0])],"isStart":false})})}),makeQuery(id+"F8.opExtrude","SWEPT_FACE",FACE,{"disambiguationData":[OSD([sQuery(id+"F7.wireOp",EDGE,"E67")])]})]});}
            var Q5;
            Q5=makeQuery(id+"F8.boolean.opBoolean","INTERSECT",EDGE,{"disambiguationData":[OD(0.0)],"derivedFrom":[makeQuery(id+"F5.opExtrude","SWEPT_FACE",FACE,{"disambiguationData":[OSD([sQuery(id+"F4.wireOp",EDGE,"E30")])]}),makeQuery(id+"F8.opExtrude","SWEPT_FACE",FACE,{"disambiguationData":[OSD([sQuery(id+"F7.wireOp",EDGE,"E67")])]})]});
            fillet(context, id + "F14", {"entities" : qUnion([Q0, Q1, Q2, Q3, Q4, Q5]), "radius" : 3 * mm, "tangentPropagation" : true, "allowEdgeOverflow" : false});
        }
        {
            var Q0;
            Q0=makeQuery(id+"F1.opExtrude","CAP_EDGE",EDGE,{"disambiguationData":[OSD([sQuery(id+"F0.wireOp",EDGE,"E1.bottom")])],"isStart":false});
            fillet(context, id + "F15", {"entities" : qUnion([Q0]), "radius" : 2 * mm, "tangentPropagation" : true, "allowEdgeOverflow" : false});
        }
        {
            var Q0;
            {var subQ0=sQuery(id+"F0.wireOp",EDGE,"E22.filletArc");var subQ1=sQuery(id+"F0.wireOp",EDGE,"E7");var subQ2=sQuery(id+"F0.wireOp",EDGE,"E6");var subQ3=sQuery(id+"F0.wireOp",EDGE,"E5");var subQ4=sQuery(id+"F0.wireOp",EDGE,"E4");var subQ5=sQuery(id+"F0.wireOp",EDGE,"E1.bottom");var subQ6=sQuery(id+"F0.wireOp",EDGE,"E21.filletArc");var subQ7=sQuery(id+"F0.wireOp",EDGE,"E1.top");var subQ8=sQuery(id+"F0.wireOp",EDGE,"E1.left");var subQ9=sQuery(id+"F0.wireOp",EDGE,"E1.right");var subQ10=sQuery(id+"F0.wireOp",EDGE,"E23.filletArc");var subQ11=sQuery(id+"F0.wireOp",EDGE,"E24.filletArc");Q0=makeQuery(id+"F2.boolean.opBoolean","SPLIT",FACE,{"disambiguationData":[TD([makeQuery(id+"F1.opExtrude","SWEPT_FACE",FACE,{"disambiguationData":[OSD([subQ5])]})])],"derivedFrom":makeQuery(id+"F1.opExtrude","CAP_FACE",FACE,{"disambiguationData":[OSD([subQ5,subQ7,subQ8,subQ9,subQ4,subQ3,subQ2,subQ1,subQ6,subQ0,subQ10,subQ11])],"isStart":true})});}
            var sketch = newSketch(context, id + "F16", { "sketchPlane" : qUnion([Q0])});
            skLineSegment(sketch, "E79", {"start": v(-33, 74.25) * mm, "end": v(-15, 92.25) * mm});
            skLineSegment(sketch, "E80", {"start": v(15, 92.25) * mm, "end": v(33, 74.25) * mm});
            skLineSegment(sketch, "E81", {"start": v(0, 104.25) * mm, "end": v(-0.8, 74.25) * mm});
            skCircle(sketch, "E82", {"center": v(0, 104.25) * mm, "radius": 6 * mm});
            skLineSegment(sketch, "E83", {"start": v(-15, 92.25) * mm, "end": v(-15, 104.25) * mm});
            skLineSegment(sketch, "E84", {"start": v(15, 92.25) * mm, "end": v(15, 104.25) * mm});
            skArc(sketch, "E85", {"start": v(15, 104.25) * mm, "mid": v(0, 119.25) * mm, "end": v(-15, 104.25) * mm});
            skLineSegment(sketch, "E86.MirrorCS", {"start": v(-33, -74.25) * mm, "end": v(-15, -92.25) * mm});
            skLineSegment(sketch, "E87.MirrorCS", {"start": v(15, -92.25) * mm, "end": v(33, -74.25) * mm});
            skLineSegment(sketch, "E88.MirrorCS", {"start": v(15, -92.25) * mm, "end": v(15, -104.25) * mm});
            skArc(sketch, "E89.MirrorCS", {"start": v(15, -104.25) * mm, "mid": v(0, -119.25) * mm, "end": v(-15, -104.25) * mm});
            skCircle(sketch, "E90.MirrorC", {"center": v(0, -104.25) * mm, "radius": 6 * mm});
            skLineSegment(sketch, "E91.MirrorCS", {"start": v(-15, -92.25) * mm, "end": v(-15, -104.25) * mm});
            skLineSegment(sketch, "E92.MirrorCS", {"start": v(0, -104.25) * mm, "end": v(-0.8, -74.25) * mm});
            skPoint(sketch, "E93.end.orphan", {"position": v(74.25, 0) * mm});
            skPoint(sketch, "E93.start.orphan", {"position": v(-74.25, 0) * mm});
            skSolve(sketch);
        }
        {
            var Q0;
            Q0=makeQuery(id+"F16.imprint","IMPRINT",FACE,{"disambiguationData":[TD([[makeQuery(id+"F16.imprint","IMPRINT",EDGE,{"derivedFrom":makeQuery(id+"F1.opExtrude","CAP_EDGE",EDGE,{"disambiguationData":[OSD([sQuery(id+"F0.wireOp",EDGE,"E1.bottom")])],"isStart":true})}),1.0]])]});
            var Q1;
            {var subQ3=sQuery(id+"F16.wireOp",EDGE,"E79");Q1=makeQuery(id+"F16.imprint","IMPRINT",FACE,{"disambiguationData":[TD([[makeQuery(id+"F16.imprint","IMPRINT",EDGE,{"derivedFrom":subQ3}),-1.0]])]});}
            var Q2;
            {var subQ1=sQuery(id+"F16.wireOp",EDGE,"RdyVCUTn-boKp-txgl-Nmpk-l3fQJCUNkRgB");Q2=makeQuery(id+"F16.imprint","IMPRINT",FACE,{"disambiguationData":[TD([[makeQuery(id+"F16.imprint","IMPRINT",EDGE,{"derivedFrom":subQ1}),1.0]])]});}
            var Q3;
            {var subQ3=sQuery(id+"F16.wireOp",EDGE,"E86.MirrorCS");Q3=makeQuery(id+"F16.imprint","IMPRINT",FACE,{"disambiguationData":[TD([[makeQuery(id+"F16.imprint","IMPRINT",EDGE,{"derivedFrom":subQ3}),1.0]])]});}
            extrude(context, id + "F17", {"entities" : qUnion([Q0, Q1, Q2, Q3]), "depth" : 3 * mm});
        }
    });
